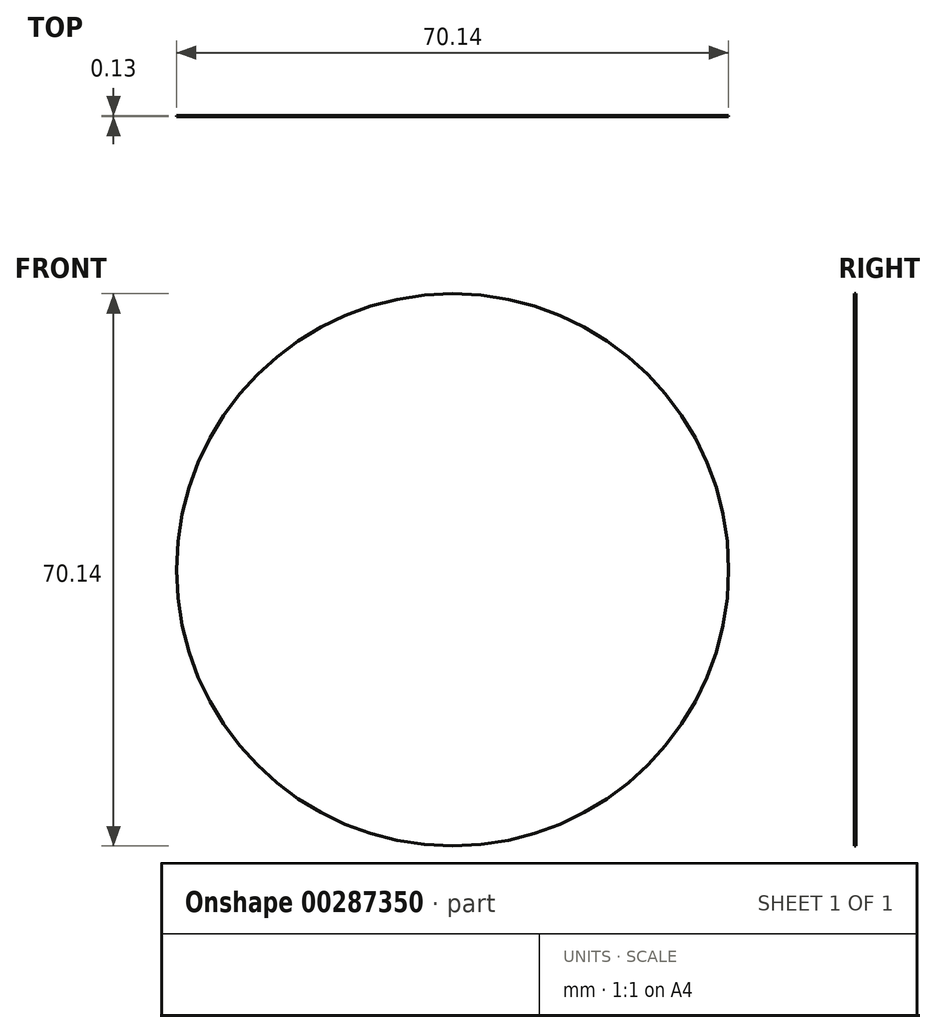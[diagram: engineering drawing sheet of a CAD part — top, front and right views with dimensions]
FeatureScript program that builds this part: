
annotation { "Feature Type Name" : "Feature", "Feature Type Description" : "" }
export const myFeature = defineFeature(function(context is Context, id is Id, definition is map)
    precondition{}
    {
        {
            var Q0;
            Q0=qCreatedBy(makeId("Front.planeOp"),FACE);
            var sketch = newSketch(context, id + "F0", { "sketchPlane" : qUnion([Q0])});
            skCircle(sketch, "E0", {"center": v(0, 0) * mm, "radius": 35.07 * mm});
            skSolve(sketch);
        }
        {
            var Q0;
            Q0=makeQuery(id+"F0.imprint","IMPRINT",FACE,{"disambiguationData":[TD([[makeQuery(id+"F0.imprint","IMPRINT",EDGE,{"derivedFrom":sQuery(id+"F0.wireOp",EDGE,"E0")}),1.0]])]});
            extrude(context, id + "F1", {"entities" : qUnion([Q0]), "depth" : 0.13 * mm});
        }
    });
